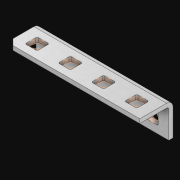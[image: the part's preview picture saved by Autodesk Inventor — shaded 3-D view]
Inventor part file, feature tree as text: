
AUTODESK INVENTOR PART (.ipt)
format: ipt  version: 2021 (Build 250183000, 183)  size: 545,280 bytes
history: native  units: in
note: dims shown in document units (in); Inventor stores cm internally (conversion verified against a paired STEP export)
features: extrude x9, other x8, sketch x3, pattern_linear x1, sheet_metal_op x1
ambient origin geometry x8: Origin, YZ Plane, XZ Plane, XY Plane, X Axis, Y Axis, Z Axis, Center Point
bodies: Solid1 (feature_tree)
feature tree (22):
  pattern_linear  "Rectangular Pattern1"  Spacing1=0.063in  [1 undecoded]
  extrude  "Extrusion1"  Depth=0.5in
  sketch  "Sketch1"  dims[d0=0.182in]
  other  "Srf1"
  sketch  "Sketch2"  dims[d1=0.063in d2=0.0in]
  other  "Srf2"
  other  "Srf3"
  other  "Srf5"
  other  "Srf7"
  other  "Srf4"
  other  "Srf6"
  other  "Srf8"
  sketch  "Sketch3"  dims[d3=0.182in d4=0.063in d5=0.0in d8=0.5in d9=15.5in d10=0.0in]
  sheet_metal_op  "Fold1"
  extrude  "ExtrusionSrf1"  Depth=0.5in TaperAngle=0.0deg
  extrude  "ExtrusionSrf2"  [1 undecoded]
  extrude  "ExtrusionSrf3"  [1 undecoded]
  extrude  "ExtrusionSrf4"  [1 undecoded]
  extrude  "ExtrusionSrf5"  [1 undecoded]
  extrude  "ExtrusionSrf37"  [1 undecoded]
  extrude  "ExtrusionSrf38"  [1 undecoded]
  extrude  "ExtrusionSrf39"  [1 undecoded]
note: 8 required parameter values undecoded (feature->parameter linkage not recoverable at this tier; creation-order binding heuristic only, values carry confidence <= 0.55)
